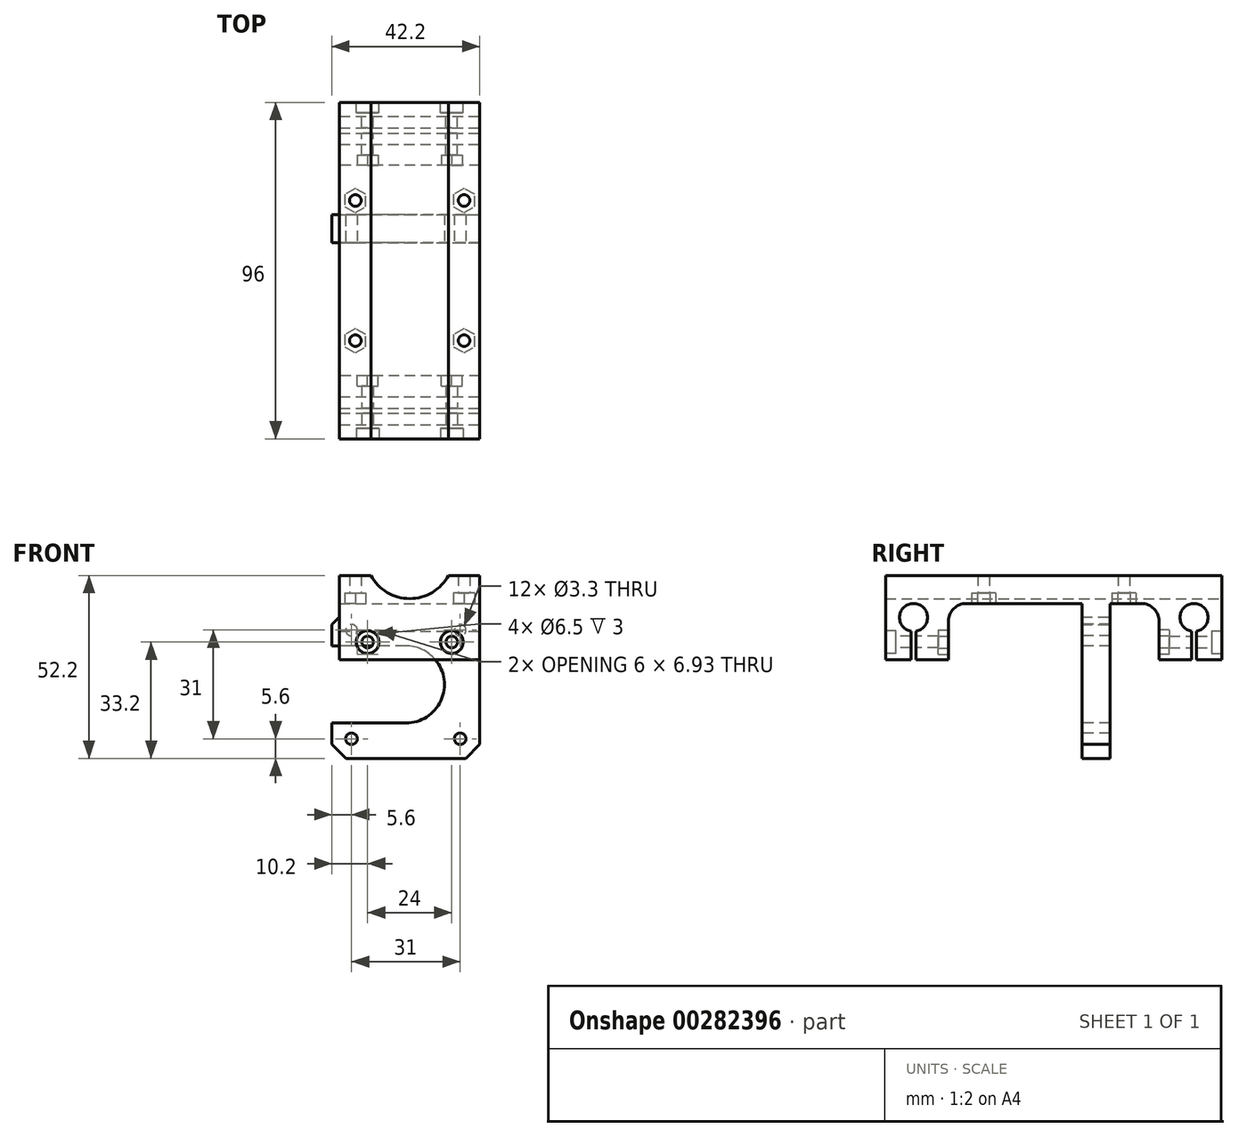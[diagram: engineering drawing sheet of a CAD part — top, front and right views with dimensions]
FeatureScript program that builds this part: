
annotation { "Feature Type Name" : "Feature", "Feature Type Description" : "" }
export const myFeature = defineFeature(function(context is Context, id is Id, definition is map)
    precondition{}
    {
        {
            var Q0;
            Q0=qCreatedBy(makeId("Front.planeOp"),FACE);
            var sketch = newSketch(context, id + "F0", { "sketchPlane" : qUnion([Q0])});
            skLineSegment(sketch, "E0.bottom", {"start": v(0, 0) * mm, "end": v(40, 0) * mm});
            skLineSegment(sketch, "E0.left", {"start": v(0, 0) * mm, "end": v(0, 24) * mm});
            skLineSegment(sketch, "E0.right", {"start": v(40, 0) * mm, "end": v(40, 24) * mm});
            skArc(sketch, "E1", {"start": v(8.92, 24) * mm, "mid": v(20, 17.4) * mm, "end": v(31.08, 24) * mm});
            skLineSegment(sketch, "E2", {"start": v(20, 30) * mm, "end": v(20, 0) * mm, "construction": true});
            skLineSegment(sketch, "E3", {"start": v(0, 24) * mm, "end": v(8.92, 24) * mm});
            skPoint(sketch, "E4.orphan", {"position": v(40, 36) * mm});
            skLineSegment(sketch, "E5.trimOffspring", {"start": v(31.08, 24) * mm, "end": v(40, 24) * mm});
            skSolve(sketch);
        }
        {
            var Q0;
            Q0=qSketchRegion(id+"F0",true);
            extrude(context, id + "F1", {"entities" : qUnion([Q0]), "depth" : 96 * mm});
        }
        {
            var Q0;
            Q0=makeQuery(id+"F1.opExtrude","SWEPT_FACE",FACE,{"disambiguationData":[OSD([sQuery(id+"F0.wireOp",EDGE,"E0.right")])]});
            var sketch = newSketch(context, id + "F2", { "sketchPlane" : qUnion([Q0])});
            skLineSegment(sketch, "E6", {"start": v(-88, 0) * mm, "end": v(-88, 0) * mm});
            skLineSegment(sketch, "E7", {"start": v(-8, 0) * mm, "end": v(-8, 0) * mm});
            skArc(sketch, "E8", {"start": v(-87.25, 8.07) * mm, "mid": v(-88, 16) * mm, "end": v(-88.75, 8.07) * mm});
            skArc(sketch, "E9", {"start": v(-7.25, 8.07) * mm, "mid": v(-8, 16) * mm, "end": v(-8.75, 8.07) * mm});
            skLineSegment(sketch, "E10.0", {"start": v(-87.25, 8.07) * mm, "end": v(-87.25, 0) * mm});
            skLineSegment(sketch, "E11.0", {"start": v(-88.75, 8.07) * mm, "end": v(-88.75, 0) * mm});
            skLineSegment(sketch, "E12.0", {"start": v(-8.75, 8.07) * mm, "end": v(-8.75, 0) * mm});
            skLineSegment(sketch, "E13.0", {"start": v(-7.25, 8.07) * mm, "end": v(-7.25, 0) * mm});
            skLineSegment(sketch, "E14", {"start": v(-8.75, 0) * mm, "end": v(-7.25, 0) * mm});
            skLineSegment(sketch, "E15", {"start": v(-88.75, 0) * mm, "end": v(-87.25, 0) * mm});
            skSolve(sketch);
        }
        {
            var Q0;
            Q0=qSketchRegion(id+"F2",true);
            extrude(context, id + "F3", {"entities" : qUnion([Q0]), "operationType" : NewBodyOperationType.REMOVE, "endBound" : BoundingType.THROUGH_ALL, "oppositeDirection" : true, "depth" : 25 * mm});
        }
        {
            var Q0;
            Q0=makeQuery(id+"F1.opExtrude","CAP_FACE",FACE,{"disambiguationData":[OSD([sQuery(id+"F0.wireOp",EDGE,"E0.bottom"),sQuery(id+"F0.wireOp",EDGE,"E0.top"),sQuery(id+"F0.wireOp",EDGE,"E0.left"),sQuery(id+"F0.wireOp",EDGE,"E0.right"),sQuery(id+"F0.wireOp",EDGE,"E1"),sQuery(id+"F0.wireOp",EDGE,"cfd72ee2-45f9-4db3-9dfb-45382d6d7eb0.trimOffspring")])],"isStart":true});
            var sketch = newSketch(context, id + "F4", { "sketchPlane" : qUnion([Q0])});
            skLineSegment(sketch, "E16", {"start": v(-40, 5) * mm, "end": v(0, 5) * mm, "construction": true});
            skLineSegment(sketch, "E17", {"start": v(-20, 0) * mm, "end": v(-20, 17.4) * mm, "construction": true});
            skPoint(sketch, "E18", {"position": v(-32, 5) * mm});
            skPoint(sketch, "E19", {"position": v(-8, 5) * mm});
            skSolve(sketch);
        }
        {
            var Q0;
            Q0=makeQuery(id+"F1.opExtrude","CAP_FACE",FACE,{"disambiguationData":[OSD([sQuery(id+"F0.wireOp",EDGE,"E0.bottom"),sQuery(id+"F0.wireOp",EDGE,"E0.top"),sQuery(id+"F0.wireOp",EDGE,"E0.left"),sQuery(id+"F0.wireOp",EDGE,"E0.right"),sQuery(id+"F0.wireOp",EDGE,"E1"),sQuery(id+"F0.wireOp",EDGE,"cfd72ee2-45f9-4db3-9dfb-45382d6d7eb0.trimOffspring")])],"isStart":false});
            var sketch = newSketch(context, id + "F5", { "sketchPlane" : qUnion([Q0])});
            skLineSegment(sketch, "E20", {"start": v(0, 5) * mm, "end": v(40, 5) * mm, "construction": true});
            skLineSegment(sketch, "E21", {"start": v(20, 0) * mm, "end": v(20, 17.4) * mm, "construction": true});
            skPoint(sketch, "E22", {"position": v(8, 5) * mm});
            skPoint(sketch, "E23", {"position": v(32, 5) * mm});
            skSolve(sketch);
        }
        {
            var Q0;
            Q0=sQuery(id+"F5.wireOp",VERTEX,"E22");
            var Q1;
            Q1=sQuery(id+"F5.wireOp",VERTEX,"E23");
            var Q2;
            Q2=sQuery(id+"F4.wireOp",VERTEX,"E19");
            var Q3;
            Q3=sQuery(id+"F4.wireOp",VERTEX,"E18");
            var Q4;
            Q4=makeQuery(id+"F1.opExtrude","SWEPT_BODY",BODY,{"disambiguationData":[OSD([sQuery(id+"F0.wireOp",EDGE,"E0.bottom"),sQuery(id+"F0.wireOp",EDGE,"E0.top"),sQuery(id+"F0.wireOp",EDGE,"E0.left"),sQuery(id+"F0.wireOp",EDGE,"E0.right"),sQuery(id+"F0.wireOp",EDGE,"E1"),sQuery(id+"F0.wireOp",EDGE,"cfd72ee2-45f9-4db3-9dfb-45382d6d7eb0.trimOffspring")])]});
            hole(context, id + "F6", {"style" : HoleStyle.C_BORE, "endStyle" : HoleEndStyle.BLIND, "standardTappedOrClearance" : lookupTablePath({ "standard" : "ISO", "fit" : "Normal", "size" : "M3", "type" : "Clearance" }), "standardBlindInLast" : lookupTablePath({ "fit" : "Standard", "standard" : "ISO", "size" : "M3", "type" : "Clearance" }), "holeDiameter" : 3.3 * mm, "cBoreDiameter" : 6.5 * mm, "cBoreDepth" : 3 * mm, "holeDepth" : 30 * mm, "tappedDepth" : 3 * mm, "tapClearance" : 3, "startFromSketch" : true, "locations" : qUnion([Q0, Q1, Q2, Q3]), "scope" : qUnion([Q4])});
        }
        {
            var Q0;
            Q0=makeQuery(id+"F1.opExtrude","SWEPT_FACE",FACE,{"disambiguationData":[OSD([sQuery(id+"F0.wireOp",EDGE,"E0.left")])]});
            var sketch = newSketch(context, id + "F7", { "sketchPlane" : qUnion([Q0])});
            skLineSegment(sketch, "E24.bottom", {"start": v(18, 0) * mm, "end": v(78, 0) * mm});
            skLineSegment(sketch, "E24.top", {"start": v(23, 16) * mm, "end": v(73, 16) * mm});
            skLineSegment(sketch, "E24.left", {"start": v(18, 0) * mm, "end": v(18, 11) * mm});
            skLineSegment(sketch, "E24.right", {"start": v(78, 0) * mm, "end": v(78, 11) * mm});
            skPoint(sketch, "E25.visualSharp", {"position": v(18, 16) * mm});
            skArc(sketch, "E25.filletArc", {"start": v(23, 16) * mm, "mid": v(19.46, 14.54) * mm, "end": v(18, 11) * mm});
            skPoint(sketch, "E26.visualSharp", {"position": v(78, 16) * mm});
            skArc(sketch, "E26.filletArc", {"start": v(78, 11) * mm, "mid": v(76.54, 14.54) * mm, "end": v(73, 16) * mm});
            skSolve(sketch);
        }
        {
            var Q0;
            Q0=qSketchRegion(id+"F7",true);
            extrude(context, id + "F8", {"entities" : qUnion([Q0]), "operationType" : NewBodyOperationType.REMOVE, "endBound" : BoundingType.THROUGH_ALL, "oppositeDirection" : true, "depth" : 25 * mm});
        }
        {
            var Q0;
            Q0=makeQuery(id+"F8.boolean.opBoolean","COPY",FACE,{"derivedFrom":makeQuery(id+"F8.opExtrude","SWEPT_FACE",FACE,{"disambiguationData":[OSD([sQuery(id+"F7.wireOp",EDGE,"E24.top")])]})});
            var sketch = newSketch(context, id + "F9", { "sketchPlane" : qUnion([Q0])});
            skLineSegment(sketch, "E27", {"start": v(0, 48) * mm, "end": v(40, 48) * mm, "construction": true});
            skLineSegment(sketch, "E28", {"start": v(4.5, 73) * mm, "end": v(4.5, 23) * mm, "construction": true});
            skLineSegment(sketch, "E29", {"start": v(35.5, 73) * mm, "end": v(35.5, 23) * mm, "construction": true});
            skCircle(sketch, "E30.cCircle", {"center": v(4.5, 68) * mm, "radius": 3 * mm, "construction": true});
            skLineSegment(sketch, "E30.0", {"start": v(7.5, 69.73) * mm, "end": v(7.5, 66.27) * mm});
            skLineSegment(sketch, "E30.1", {"start": v(7.5, 66.27) * mm, "end": v(4.5, 64.54) * mm});
            skLineSegment(sketch, "E30.2", {"start": v(4.5, 64.54) * mm, "end": v(1.5, 66.27) * mm});
            skLineSegment(sketch, "E30.3", {"start": v(1.5, 66.27) * mm, "end": v(1.5, 69.73) * mm});
            skLineSegment(sketch, "E30.4", {"start": v(1.5, 69.73) * mm, "end": v(4.5, 71.46) * mm});
            skLineSegment(sketch, "E30.5", {"start": v(4.5, 71.46) * mm, "end": v(7.5, 69.73) * mm});
            skPoint(sketch, "E30.0.midPoint", {"position": v(7.5, 68) * mm});
            skCircle(sketch, "E31.cCircle", {"center": v(35.5, 68) * mm, "radius": 3 * mm, "construction": true});
            skLineSegment(sketch, "E31.0", {"start": v(32.5, 66.27) * mm, "end": v(32.5, 69.73) * mm});
            skLineSegment(sketch, "E31.1", {"start": v(32.5, 69.73) * mm, "end": v(35.5, 71.46) * mm});
            skLineSegment(sketch, "E31.2", {"start": v(35.5, 71.46) * mm, "end": v(38.5, 69.73) * mm});
            skLineSegment(sketch, "E31.3", {"start": v(38.5, 69.73) * mm, "end": v(38.5, 66.27) * mm});
            skLineSegment(sketch, "E31.4", {"start": v(38.5, 66.27) * mm, "end": v(35.5, 64.54) * mm});
            skLineSegment(sketch, "E31.5", {"start": v(35.5, 64.54) * mm, "end": v(32.5, 66.27) * mm});
            skPoint(sketch, "E31.0.midPoint", {"position": v(32.5, 68) * mm});
            skCircle(sketch, "E32.cCircle", {"center": v(4.5, 28) * mm, "radius": 3 * mm, "construction": true});
            skLineSegment(sketch, "E32.0", {"start": v(7.5, 29.73) * mm, "end": v(7.5, 26.27) * mm});
            skLineSegment(sketch, "E32.1", {"start": v(7.5, 26.27) * mm, "end": v(4.5, 24.54) * mm});
            skLineSegment(sketch, "E32.2", {"start": v(4.5, 24.54) * mm, "end": v(1.5, 26.27) * mm});
            skLineSegment(sketch, "E32.3", {"start": v(1.5, 26.27) * mm, "end": v(1.5, 29.73) * mm});
            skLineSegment(sketch, "E32.4", {"start": v(1.5, 29.73) * mm, "end": v(4.5, 31.46) * mm});
            skLineSegment(sketch, "E32.5", {"start": v(4.5, 31.46) * mm, "end": v(7.5, 29.73) * mm});
            skPoint(sketch, "E32.0.midPoint", {"position": v(7.5, 28) * mm});
            skCircle(sketch, "E33.cCircle", {"center": v(35.5, 28) * mm, "radius": 3 * mm, "construction": true});
            skLineSegment(sketch, "E33.0", {"start": v(32.5, 26.27) * mm, "end": v(32.5, 29.73) * mm});
            skLineSegment(sketch, "E33.1", {"start": v(32.5, 29.73) * mm, "end": v(35.5, 31.46) * mm});
            skLineSegment(sketch, "E33.2", {"start": v(35.5, 31.46) * mm, "end": v(38.5, 29.73) * mm});
            skLineSegment(sketch, "E33.3", {"start": v(38.5, 29.73) * mm, "end": v(38.5, 26.27) * mm});
            skLineSegment(sketch, "E33.4", {"start": v(38.5, 26.27) * mm, "end": v(35.5, 24.54) * mm});
            skLineSegment(sketch, "E33.5", {"start": v(35.5, 24.54) * mm, "end": v(32.5, 26.27) * mm});
            skPoint(sketch, "E33.0.midPoint", {"position": v(32.5, 28) * mm});
            skLineSegment(sketch, "E34", {"start": v(4.5, 28) * mm, "end": v(7.5, 28) * mm, "construction": true});
            skLineSegment(sketch, "E35", {"start": v(7.5, 68) * mm, "end": v(4.5, 68) * mm, "construction": true});
            skLineSegment(sketch, "E36", {"start": v(32.5, 28) * mm, "end": v(35.5, 28) * mm, "construction": true});
            skLineSegment(sketch, "E37", {"start": v(32.5, 68) * mm, "end": v(35.5, 68) * mm, "construction": true});
            skSolve(sketch);
        }
        {
            var Q0;
            Q0=qSketchRegion(id+"F9",true);
            extrude(context, id + "F10", {"entities" : qUnion([Q0]), "operationType" : NewBodyOperationType.REMOVE, "oppositeDirection" : true, "depth" : 3 * mm});
        }
        {
            var Q0;
            Q0=makeQuery(id+"F8.boolean.opBoolean","COPY",FACE,{"derivedFrom":makeQuery(id+"F8.opExtrude","SWEPT_FACE",FACE,{"disambiguationData":[OSD([sQuery(id+"F7.wireOp",EDGE,"E24.left")])]})});
            var sketch = newSketch(context, id + "F11", { "sketchPlane" : qUnion([Q0])});
            skCircle(sketch, "E38.cCircle", {"center": v(8, 5) * mm, "radius": 3 * mm, "construction": true});
            skLineSegment(sketch, "E38.0", {"start": v(11, 6.73) * mm, "end": v(11, 3.27) * mm});
            skLineSegment(sketch, "E38.1", {"start": v(11, 3.27) * mm, "end": v(8, 1.54) * mm});
            skLineSegment(sketch, "E38.2", {"start": v(8, 1.54) * mm, "end": v(5, 3.27) * mm});
            skLineSegment(sketch, "E38.3", {"start": v(5, 3.27) * mm, "end": v(5, 6.73) * mm});
            skLineSegment(sketch, "E38.4", {"start": v(5, 6.73) * mm, "end": v(8, 8.46) * mm});
            skLineSegment(sketch, "E38.5", {"start": v(8, 8.46) * mm, "end": v(11, 6.73) * mm});
            skPoint(sketch, "E38.0.midPoint", {"position": v(11, 5) * mm});
            skCircle(sketch, "E39.cCircle", {"center": v(32, 5) * mm, "radius": 3 * mm, "construction": true});
            skLineSegment(sketch, "E39.0", {"start": v(35, 6.73) * mm, "end": v(35, 3.27) * mm});
            skLineSegment(sketch, "E39.1", {"start": v(35, 3.27) * mm, "end": v(32, 1.54) * mm});
            skLineSegment(sketch, "E39.2", {"start": v(32, 1.54) * mm, "end": v(29, 3.27) * mm});
            skLineSegment(sketch, "E39.3", {"start": v(29, 3.27) * mm, "end": v(29, 6.73) * mm});
            skLineSegment(sketch, "E39.4", {"start": v(29, 6.73) * mm, "end": v(32, 8.46) * mm});
            skLineSegment(sketch, "E39.5", {"start": v(32, 8.46) * mm, "end": v(35, 6.73) * mm});
            skPoint(sketch, "E39.0.midPoint", {"position": v(35, 5) * mm});
            skLineSegment(sketch, "E40", {"start": v(32, 5) * mm, "end": v(35, 5) * mm, "construction": true});
            skLineSegment(sketch, "E41", {"start": v(8, 5) * mm, "end": v(11, 5) * mm, "construction": true});
            skSolve(sketch);
        }
        {
            var Q0;
            Q0=qSketchRegion(id+"F11",true);
            extrude(context, id + "F12", {"entities" : qUnion([Q0]), "operationType" : NewBodyOperationType.REMOVE, "oppositeDirection" : true, "depth" : 3 * mm});
        }
        {
            var Q0;
            Q0=makeQuery(id+"F8.boolean.opBoolean","COPY",FACE,{"derivedFrom":makeQuery(id+"F8.opExtrude","SWEPT_FACE",FACE,{"disambiguationData":[OSD([sQuery(id+"F7.wireOp",EDGE,"E24.right")])]})});
            var sketch = newSketch(context, id + "F13", { "sketchPlane" : qUnion([Q0])});
            skCircle(sketch, "E42.cCircle", {"center": v(-32, 5) * mm, "radius": 3 * mm, "construction": true});
            skLineSegment(sketch, "E42.0", {"start": v(-35, 3.27) * mm, "end": v(-35, 6.73) * mm});
            skLineSegment(sketch, "E42.1", {"start": v(-35, 6.73) * mm, "end": v(-32, 8.46) * mm});
            skLineSegment(sketch, "E42.2", {"start": v(-32, 8.46) * mm, "end": v(-29, 6.73) * mm});
            skLineSegment(sketch, "E42.3", {"start": v(-29, 6.73) * mm, "end": v(-29, 3.27) * mm});
            skLineSegment(sketch, "E42.4", {"start": v(-29, 3.27) * mm, "end": v(-32, 1.54) * mm});
            skLineSegment(sketch, "E42.5", {"start": v(-32, 1.54) * mm, "end": v(-35, 3.27) * mm});
            skPoint(sketch, "E42.0.midPoint", {"position": v(-35, 5) * mm});
            skCircle(sketch, "E43.cCircle", {"center": v(-8, 5) * mm, "radius": 3 * mm, "construction": true});
            skLineSegment(sketch, "E43.0", {"start": v(-11, 3.27) * mm, "end": v(-11, 6.73) * mm});
            skLineSegment(sketch, "E43.1", {"start": v(-11, 6.73) * mm, "end": v(-8, 8.46) * mm});
            skLineSegment(sketch, "E43.2", {"start": v(-8, 8.46) * mm, "end": v(-5, 6.73) * mm});
            skLineSegment(sketch, "E43.3", {"start": v(-5, 6.73) * mm, "end": v(-5, 3.27) * mm});
            skLineSegment(sketch, "E43.4", {"start": v(-5, 3.27) * mm, "end": v(-8, 1.54) * mm});
            skLineSegment(sketch, "E43.5", {"start": v(-8, 1.54) * mm, "end": v(-11, 3.27) * mm});
            skPoint(sketch, "E43.0.midPoint", {"position": v(-11, 5) * mm});
            skLineSegment(sketch, "E44", {"start": v(-11, 5) * mm, "end": v(-8, 5) * mm, "construction": true});
            skLineSegment(sketch, "E45", {"start": v(-35, 5) * mm, "end": v(-32, 5) * mm, "construction": true});
            skSolve(sketch);
        }
        {
            var Q0;
            Q0=qSketchRegion(id+"F13",true);
            extrude(context, id + "F14", {"entities" : qUnion([Q0]), "operationType" : NewBodyOperationType.REMOVE, "oppositeDirection" : true, "depth" : 3 * mm});
        }
        {
            var Q0;
            Q0=makeQuery(id+"F8.boolean.opBoolean","COPY",FACE,{"derivedFrom":makeQuery(id+"F8.opExtrude","SWEPT_FACE",FACE,{"disambiguationData":[OSD([sQuery(id+"F7.wireOp",EDGE,"E24.top")])]})});
            var sketch = newSketch(context, id + "F15", { "sketchPlane" : qUnion([Q0])});
            skLineSegment(sketch, "E46.bottom", {"start": v(0, 32) * mm, "end": v(40, 32) * mm});
            skLineSegment(sketch, "E46.top", {"start": v(0, 40) * mm, "end": v(40, 40) * mm});
            skLineSegment(sketch, "E46.left", {"start": v(0, 32) * mm, "end": v(0, 40) * mm});
            skLineSegment(sketch, "E46.right", {"start": v(40, 32) * mm, "end": v(40, 40) * mm});
            skSolve(sketch);
        }
        {
            var Q0;
            Q0=qSketchRegion(id+"F15",true);
            extrude(context, id + "F16", {"entities" : qUnion([Q0]), "operationType" : NewBodyOperationType.ADD, "depth" : 2 * mm});
        }
        {
            var Q0;
            Q0=makeQuery(id+"F16.opExtrude","SWEPT_FACE",FACE,{"disambiguationData":[OSD([sQuery(id+"F15.wireOp",EDGE,"E46.top")])]});
            var sketch = newSketch(context, id + "F17", { "sketchPlane" : qUnion([Q0])});
            skLineSegment(sketch, "E47", {"start": v(40, 14) * mm, "end": v(40, -28.2) * mm});
            skLineSegment(sketch, "E48", {"start": v(40, -28.2) * mm, "end": v(-2.2, -28.2) * mm});
            skLineSegment(sketch, "E49", {"start": v(-2.2, -28.2) * mm, "end": v(-2.2, -18.1) * mm});
            skLineSegment(sketch, "E50", {"start": v(-2.2, 14) * mm, "end": v(40, -28.2) * mm, "construction": true});
            skArc(sketch, "E51", {"start": v(18.9, -18.1) * mm, "mid": v(29.9, -7.1) * mm, "end": v(18.9, 3.9) * mm});
            skLineSegment(sketch, "E52", {"start": v(-2.2, 14) * mm, "end": v(40, 14) * mm});
            skLineSegment(sketch, "E53", {"start": v(40, 14) * mm, "end": v(-2.2, -28.2) * mm, "construction": true});
            skCircle(sketch, "E54", {"center": v(3.4, 8.4) * mm, "radius": 1.65 * mm});
            skCircle(sketch, "E55", {"center": v(34.4, 8.4) * mm, "radius": 1.65 * mm});
            skCircle(sketch, "E56", {"center": v(34.4, -22.6) * mm, "radius": 1.65 * mm});
            skCircle(sketch, "E57", {"center": v(3.4, -22.6) * mm, "radius": 1.65 * mm});
            skLineSegment(sketch, "E58", {"start": v(18.9, -28.2) * mm, "end": v(18.9, 14) * mm, "construction": true});
            skLineSegment(sketch, "E59", {"start": v(18.9, 3.9) * mm, "end": v(-2.2, 3.9) * mm});
            skLineSegment(sketch, "E60", {"start": v(18.9, -18.1) * mm, "end": v(-2.2, -18.1) * mm});
            skLineSegment(sketch, "E61.trimOffspring", {"start": v(-2.2, 3.9) * mm, "end": v(-2.2, 14) * mm});
            skSolve(sketch);
        }
        {
            var Q0;
            Q0=qSketchRegion(id+"F17",true);
            extrude(context, id + "F18", {"entities" : qUnion([Q0]), "oppositeDirection" : true, "depth" : 8 * mm});
        }
        {
            var Q0;
            Q0=makeQuery(id+"F1.opExtrude","SWEPT_BODY",BODY,{"disambiguationData":[OSD([sQuery(id+"F0.wireOp",EDGE,"E0.bottom"),sQuery(id+"F0.wireOp",EDGE,"E0.top"),sQuery(id+"F0.wireOp",EDGE,"E0.left"),sQuery(id+"F0.wireOp",EDGE,"E0.right"),sQuery(id+"F0.wireOp",EDGE,"E1"),sQuery(id+"F0.wireOp",EDGE,"cfd72ee2-45f9-4db3-9dfb-45382d6d7eb0.trimOffspring")])]});
            var Q1;
            Q1=makeQuery(id+"F18.opExtrude","SWEPT_BODY",BODY,{"disambiguationData":[OSD([sQuery(id+"F17.wireOp",EDGE,"E47"),sQuery(id+"F17.wireOp",EDGE,"E48"),sQuery(id+"F17.wireOp",EDGE,"E49"),sQuery(id+"F17.wireOp",EDGE,"E51"),sQuery(id+"F17.wireOp",EDGE,"E52"),sQuery(id+"F17.wireOp",EDGE,"E54"),sQuery(id+"F17.wireOp",EDGE,"E55"),sQuery(id+"F17.wireOp",EDGE,"E56"),sQuery(id+"F17.wireOp",EDGE,"E57")])]});
            booleanBodies(context, id + "F19", {"operationType" : BooleanOperationType.UNION, "tools" : qUnion([Q0, Q1])});
        }
        {
            var Q0;
            Q0=makeQuery(id+"F18.opExtrude","SWEPT_EDGE",EDGE,{"disambiguationData":[OSD([sQuery(id+"F17.wireOp",EDGE,"E48"),sQuery(id+"F17.wireOp",EDGE,"E49")])]});
            var Q1;
            Q1=makeQuery(id+"F18.opExtrude","SWEPT_EDGE",EDGE,{"disambiguationData":[OSD([sQuery(id+"F17.wireOp",EDGE,"E47"),sQuery(id+"F17.wireOp",EDGE,"E48")])]});
            chamfer(context, id + "F20", {"entities" : qUnion([Q0, Q1]), "width" : 4 * mm, "tangentPropagation" : true});
        }
        {
            var Q0;
            Q0=makeQuery(id+"F19.opBoolean","MERGE",FACE,{"derivedFrom":[makeQuery(id+"F16.opExtrude","SWEPT_FACE",FACE,{"disambiguationData":[OSD([sQuery(id+"F15.wireOp",EDGE,"E46.bottom")])]}),makeQuery(id+"F18.opExtrude","CAP_FACE",FACE,{"disambiguationData":[OSD([sQuery(id+"F17.wireOp",EDGE,"E47"),sQuery(id+"F17.wireOp",EDGE,"E48"),sQuery(id+"F17.wireOp",EDGE,"E49"),sQuery(id+"F17.wireOp",EDGE,"E51"),sQuery(id+"F17.wireOp",EDGE,"E52"),sQuery(id+"F17.wireOp",EDGE,"E54"),sQuery(id+"F17.wireOp",EDGE,"E55"),sQuery(id+"F17.wireOp",EDGE,"E56"),sQuery(id+"F17.wireOp",EDGE,"E57")])],"isStart":false})]});
            var sketch = newSketch(context, id + "F21", { "sketchPlane" : qUnion([Q0])});
            skLineSegment(sketch, "E62", {"start": v(0, 14) * mm, "end": v(0, 12.2) * mm});
            skLineSegment(sketch, "E63", {"start": v(0, 12.2) * mm, "end": v(2.2, 10) * mm});
            skLineSegment(sketch, "E64", {"start": v(2.2, 10) * mm, "end": v(3.2, 10) * mm});
            skLineSegment(sketch, "E65", {"start": v(3.2, 10) * mm, "end": v(3.2, 15) * mm});
            skLineSegment(sketch, "E66", {"start": v(3.2, 15) * mm, "end": v(0, 15) * mm});
            skLineSegment(sketch, "E67", {"start": v(0, 15) * mm, "end": v(0, 14) * mm});
            skSolve(sketch);
        }
        {
            var Q0;
            Q0=qSketchRegion(id+"F21",true);
            extrude(context, id + "F22", {"entities" : qUnion([Q0]), "operationType" : NewBodyOperationType.REMOVE, "endBound" : BoundingType.THROUGH_ALL, "oppositeDirection" : true, "depth" : 25 * mm});
        }
        {
            var Q0;
            Q0=makeQuery(id+"F16.boolean.opBoolean","SPLIT",FACE,{"disambiguationData":[TD([makeQuery(id+"F8.boolean.opBoolean","COPY",FACE,{"derivedFrom":makeQuery(id+"F8.opExtrude","SWEPT_FACE",FACE,{"disambiguationData":[OSD([sQuery(id+"F7.wireOp",EDGE,"E26.filletArc")])]})})])],"derivedFrom":makeQuery(id+"F8.boolean.opBoolean","COPY",FACE,{"derivedFrom":makeQuery(id+"F8.opExtrude","SWEPT_FACE",FACE,{"disambiguationData":[OSD([sQuery(id+"F7.wireOp",EDGE,"E24.top")])]})})});
            var sketch = newSketch(context, id + "F23", { "sketchPlane" : qUnion([Q0])});
            skLineSegment(sketch, "E68", {"start": v(20, 73) * mm, "end": v(20, 23) * mm, "construction": true});
            skLineSegment(sketch, "E69", {"start": v(20, 48) * mm, "end": v(40, 48) * mm, "construction": true});
            skCircle(sketch, "E70", {"center": v(35.5, 68) * mm, "radius": 1.65 * mm});
            skCircle(sketch, "E71", {"center": v(4.5, 68) * mm, "radius": 1.65 * mm});
            skPoint(sketch, "E71.centerSnap0", {"position": v(7.5, 68) * mm});
            skCircle(sketch, "E72", {"center": v(35.5, 28) * mm, "radius": 1.65 * mm});
            skCircle(sketch, "E73", {"center": v(4.5, 28) * mm, "radius": 1.65 * mm});
            skSolve(sketch);
        }
        {
            var Q0;
            Q0=qSketchRegion(id+"F23",true);
            extrude(context, id + "F24", {"entities" : qUnion([Q0]), "operationType" : NewBodyOperationType.REMOVE, "oppositeDirection" : true, "depth" : 25 * mm});
        }
    });
